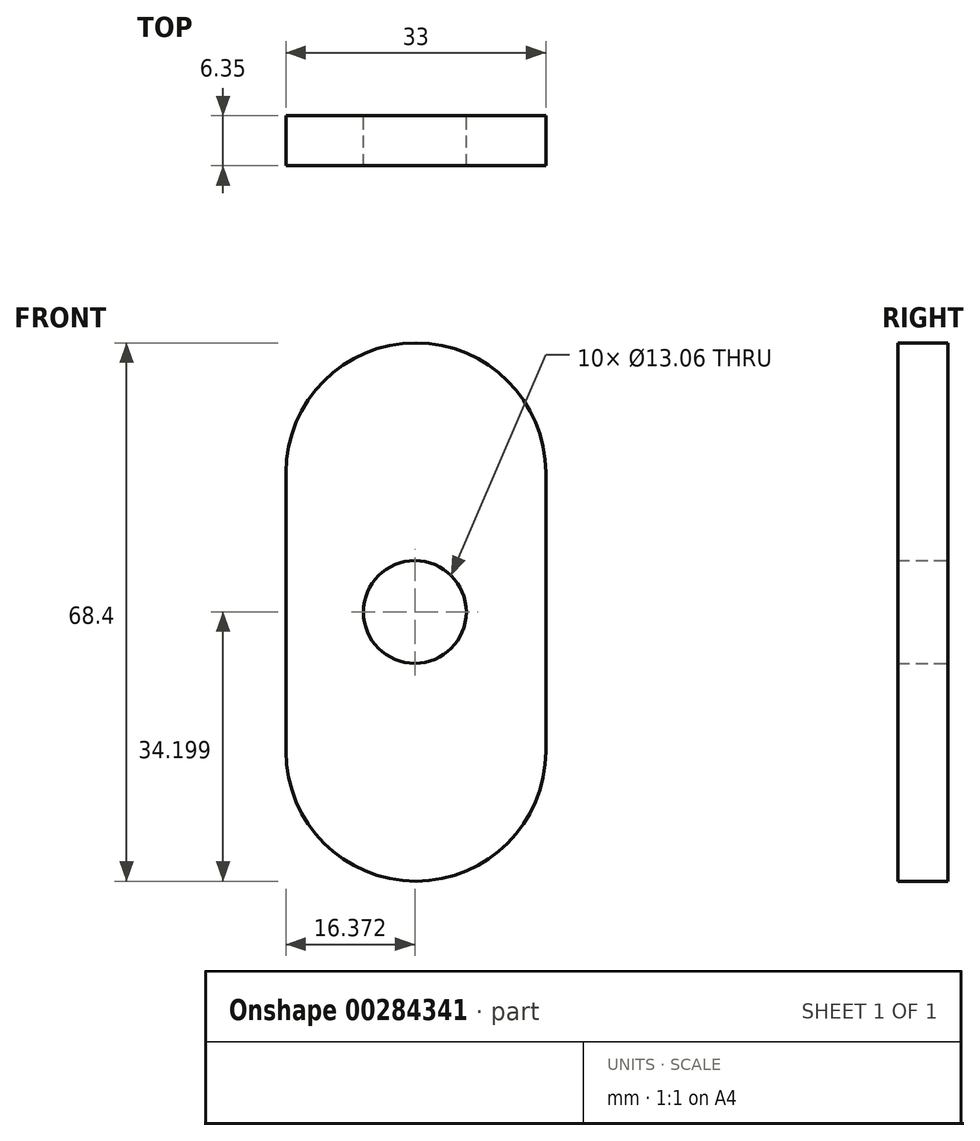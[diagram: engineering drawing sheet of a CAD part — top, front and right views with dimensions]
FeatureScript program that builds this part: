
annotation { "Feature Type Name" : "Feature", "Feature Type Description" : "" }
export const myFeature = defineFeature(function(context is Context, id is Id, definition is map)
    precondition{}
    {
        {
            var Q0;
            Q0=qCreatedBy(makeId("Front.planeOp"),FACE);
            var sketch = newSketch(context, id + "F0", { "sketchPlane" : qUnion([Q0])});
            skLineSegment(sketch, "E0", {"start": v(-55.86, 40.93) * mm, "end": v(-55.86, 5.53) * mm});
            skArc(sketch, "E1", {"start": v(-55.86, 5.53) * mm, "mid": v(-39.36, -10.97) * mm, "end": v(-22.86, 5.53) * mm});
            skLineSegment(sketch, "E2.MirrorCS", {"start": v(-22.86, 40.93) * mm, "end": v(-22.86, 5.53) * mm});
            skArc(sketch, "E3.MirrorCS", {"start": v(-22.86, 5.53) * mm, "mid": v(-39.36, -10.97) * mm, "end": v(-55.86, 5.53) * mm});
            skLineSegment(sketch, "E4", {"start": v(-67.66, 23.23) * mm, "end": v(3.13, 23.23) * mm, "construction": true});
            skArc(sketch, "E5.MirrorCS", {"start": v(-22.86, 40.93) * mm, "mid": v(-39.36, 57.43) * mm, "end": v(-55.86, 40.93) * mm});
            skLineSegment(sketch, "E6.MirrorCS", {"start": v(-55.86, 5.53) * mm, "end": v(-55.86, 40.93) * mm});
            skLineSegment(sketch, "E7.MirrorCS", {"start": v(-22.86, 5.53) * mm, "end": v(-22.86, 40.93) * mm});
            skPoint(sketch, "E8.orphan", {"position": v(-55.86, 51.62) * mm});
            skPoint(sketch, "E9.orphan", {"position": v(-22.86, 51.62) * mm});
            skPoint(sketch, "E10.orphan", {"position": v(-22.86, -5.16) * mm});
            skPoint(sketch, "E11.orphan", {"position": v(-55.86, -5.16) * mm});
            skCircle(sketch, "E12", {"center": v(-39.49, 23.23) * mm, "radius": 6.53 * mm});
            skSolve(sketch);
        }
        {
            var Q0;
            Q0 = qSketchRegion(id + "F0", true);
            extrude(context, id + "F1", {"entities" : qUnion([Q0]), "depth" : 6.35 * mm});
        }
    });
